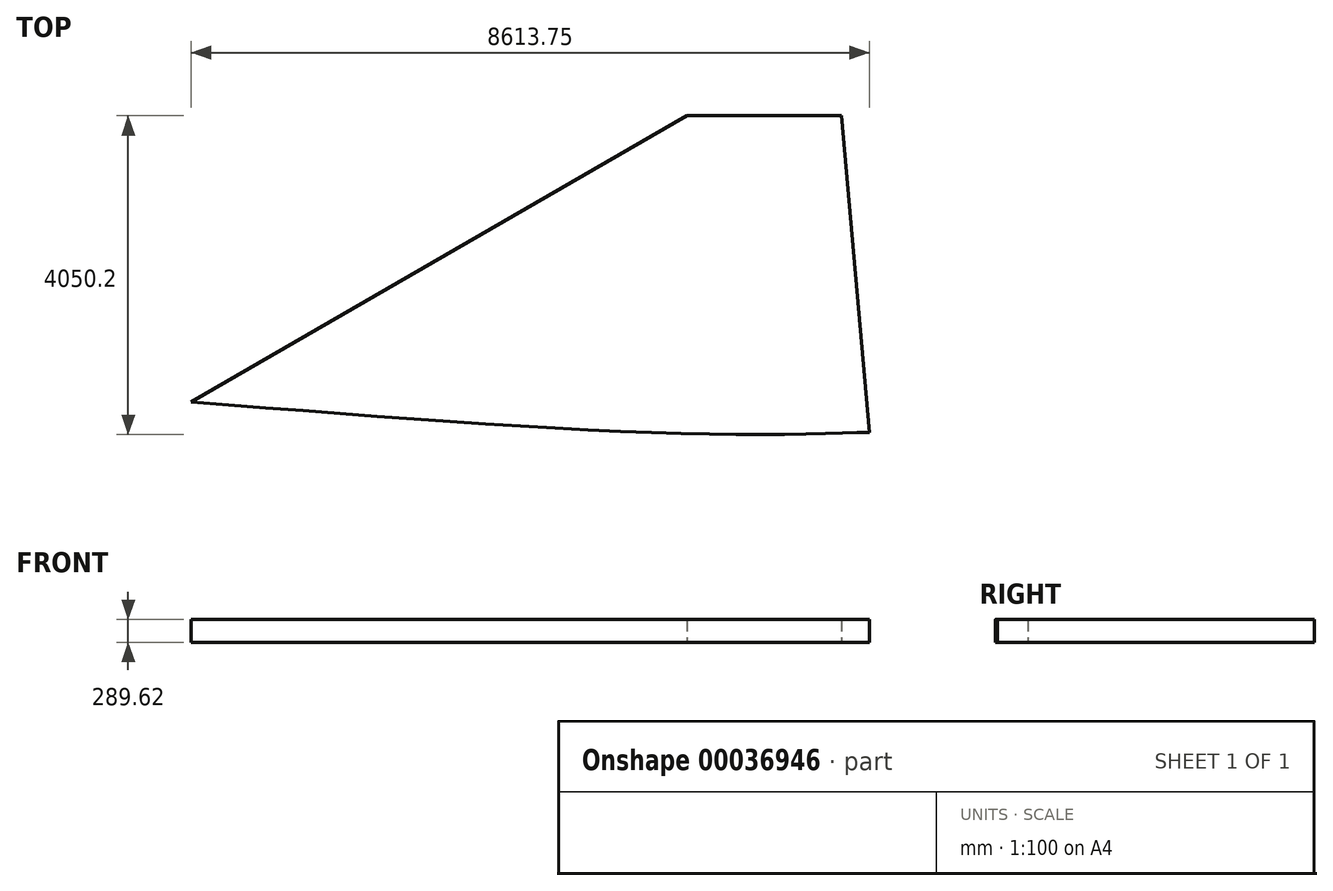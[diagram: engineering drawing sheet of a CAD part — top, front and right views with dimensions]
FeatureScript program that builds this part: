
annotation { "Feature Type Name" : "Feature", "Feature Type Description" : "" }
export const myFeature = defineFeature(function(context is Context, id is Id, definition is map)
    precondition{}
    {
        {
            var Q0;
            Q0=qCreatedBy(makeId("Top.planeOp"),FACE);
            var sketch = newSketch(context, id + "F0", { "sketchPlane" : qUnion([Q0])});
            skLineSegment(sketch, "E0", {"start": v(0, 0) * mm, "end": v(10107.64, 5835.65) * mm});
            skLineSegment(sketch, "E1", {"start": v(10861.04, 0) * mm, "end": v(0, 0) * mm});
            skLineSegment(sketch, "E2", {"start": v(10107.64, 5835.65) * mm, "end": v(10350.49, 5835.65) * mm});
            skLineSegment(sketch, "E3", {"start": v(10861.04, 0) * mm, "end": v(10350.49, 5835.65) * mm});
            skSolve(sketch);
        }
        {
            var Q0;
            Q0=makeQuery(id+"F0.imprint","IMPRINT",FACE,{"disambiguationData":[TD([[makeQuery(id+"F0.imprint","IMPRINT",EDGE,{"derivedFrom":sQuery(id+"F0.wireOp",EDGE,"E0")}),-1.0]])]});
            var sketch = newSketch(context, id + "F1", { "sketchPlane" : qUnion([Q0])});
            skLineSegment(sketch, "E4", {"start": v(2171.45, 2095.8) * mm, "end": v(2171.45, -777.95) * mm, "construction": true});
            skLineSegment(sketch, "E5", {"start": v(10861.04, 1272.68) * mm, "end": v(10861.04, -670.62) * mm, "construction": true});
            skFitSpline(sketch, "E6", {"points": [v(2171.45, 1253.68) * mm, v(8810.75, 843.79) * mm, v(10861.04, 867.4) * mm], "startDerivative": vector(11078.91, -881.61) * mm, "endDerivative": vector(2816.68, 0) * mm});
            skLineSegment(sketch, "E7", {"start": v(2171.45, 1253.68) * mm, "end": v(10107.64, 5835.65) * mm});
            skLineSegment(sketch, "E8", {"start": v(10107.64, 5835.65) * mm, "end": v(10350.49, 5835.65) * mm});
            skLineSegment(sketch, "E9", {"start": v(10350.49, 5835.65) * mm, "end": v(10785.2, 866.89) * mm});
            skSolve(sketch);
        }
        {
            var Q0;
            Q0=qSketchRegion(id+"F1",true);
            extrude(context, id + "F2", {"entities" : qUnion([Q0]), "depth" : 289.62 * mm});
        }
        {
            var Q0;
            Q0=makeQuery(id+"F2.opExtrude","CAP_FACE",FACE,{"disambiguationData":[OSD([sQuery(id+"F1.wireOp",EDGE,"E6"),sQuery(id+"F1.wireOp",EDGE,"E7"),sQuery(id+"F1.wireOp",EDGE,"E8"),sQuery(id+"F1.wireOp",EDGE,"E9")])],"isStart":false});
            var sketch = newSketch(context, id + "F3", { "sketchPlane" : qUnion([Q0])});
            skLineSegment(sketch, "E10.bottom", {"start": v(11012.82, 5835.65) * mm, "end": v(8403.66, 5835.65) * mm});
            skLineSegment(sketch, "E10.top", {"start": v(11012.82, 4890.77) * mm, "end": v(8403.66, 4890.77) * mm});
            skLineSegment(sketch, "E10.left", {"start": v(11012.82, 5835.65) * mm, "end": v(11012.82, 4890.77) * mm});
            skLineSegment(sketch, "E10.right", {"start": v(8403.66, 5835.65) * mm, "end": v(8403.66, 4890.77) * mm});
            skSolve(sketch);
        }
        {
            var Q0;
            Q0 = qSketchRegion(id + "F3", true);
            extrude(context, id + "F4", {"entities" : qUnion([Q0]), "operationType" : NewBodyOperationType.REMOVE, "endBound" : BoundingType.THROUGH_ALL, "oppositeDirection" : true, "depth" : 25.4 * mm});
        }
    });
